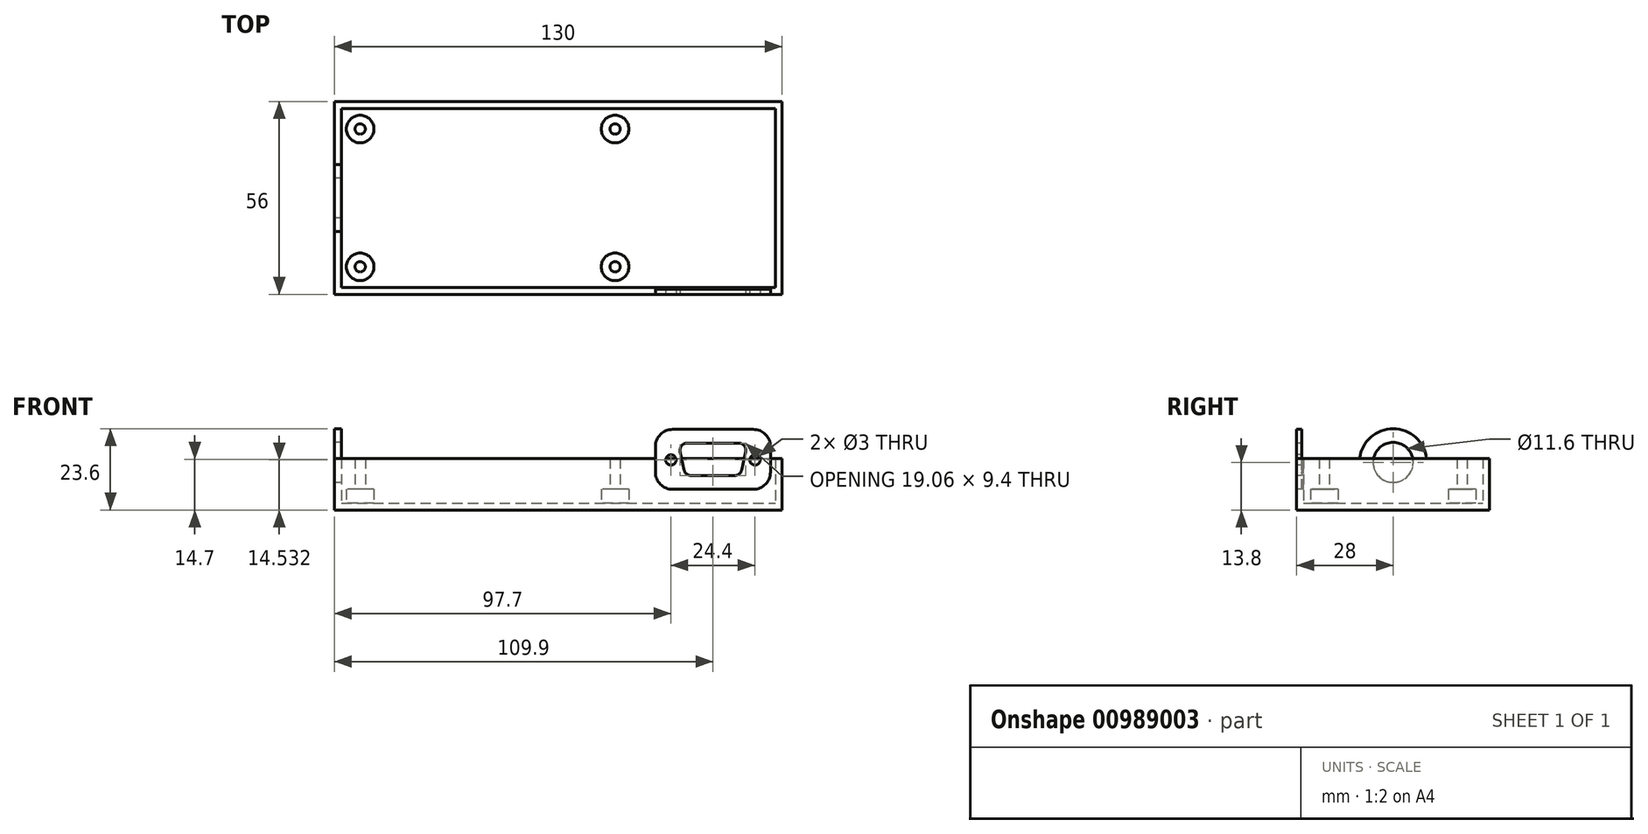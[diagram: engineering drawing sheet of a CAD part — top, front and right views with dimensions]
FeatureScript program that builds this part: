
annotation { "Feature Type Name" : "Feature", "Feature Type Description" : "" }
export const myFeature = defineFeature(function(context is Context, id is Id, definition is map)
    precondition{}
    {
        {
            var Q0;
            Q0=qCreatedBy(makeId("Top.planeOp"),FACE);
            var sketch = newSketch(context, id + "F0", { "sketchPlane" : qUnion([Q0])});
            skLineSegment(sketch, "E0.bottom", {"start": v(0, 0) * mm, "end": v(130, 0) * mm});
            skLineSegment(sketch, "E0.top", {"start": v(0, 56) * mm, "end": v(130, 56) * mm});
            skLineSegment(sketch, "E0.left", {"start": v(0, 0) * mm, "end": v(0, 56) * mm});
            skLineSegment(sketch, "E0.right", {"start": v(130, 0) * mm, "end": v(130, 56) * mm});
            skSolve(sketch);
        }
        {
            var Q0;
            Q0=makeQuery(id+"F0.imprint","IMPRINT",FACE,{"disambiguationData":[TD([[makeQuery(id+"F0.imprint","IMPRINT",EDGE,{"derivedFrom":sQuery(id+"F0.wireOp",EDGE,"E0.bottom")}),1.0]])]});
            extrude(context, id + "F1", {"entities" : qUnion([Q0]), "depth" : 15 * mm, "offsetDistance" : 25 * mm});
        }
        {
            var Q0;
            Q0=makeQuery(id+"F1.opExtrude","CAP_FACE",FACE,{"disambiguationData":[OSD([sQuery(id+"F0.wireOp",EDGE,"E0.bottom"),sQuery(id+"F0.wireOp",EDGE,"E0.top"),sQuery(id+"F0.wireOp",EDGE,"E0.left"),sQuery(id+"F0.wireOp",EDGE,"E0.right")])],"isStart":false});
            shell(context, id + "F2", {"entities" : qUnion([Q0]), "thickness" : 2 * mm});
        }
        {
            var Q0;
            Q0=makeQuery(id+"F2.opShell","OFFSET_FACE",FACE,{"disambiguationData":[OSD([sQuery(id+"F0.wireOp",EDGE,"E0.bottom"),sQuery(id+"F0.wireOp",EDGE,"E0.top"),sQuery(id+"F0.wireOp",EDGE,"E0.left"),sQuery(id+"F0.wireOp",EDGE,"E0.right")])]});
            var sketch = newSketch(context, id + "F3", { "sketchPlane" : qUnion([Q0])});
            skLineSegment(sketch, "E1.bottom", {"start": v(2.5, 53) * mm, "end": v(86.5, 53) * mm, "construction": true});
            skLineSegment(sketch, "E1.top", {"start": v(2.5, 3) * mm, "end": v(86.5, 3) * mm, "construction": true});
            skLineSegment(sketch, "E1.left", {"start": v(2.5, 53) * mm, "end": v(2.5, 3) * mm, "construction": true});
            skLineSegment(sketch, "E1.right", {"start": v(86.5, 53) * mm, "end": v(86.5, 3) * mm, "construction": true});
            skCircle(sketch, "E2", {"center": v(81.5, 48) * mm, "radius": 1.5 * mm});
            skCircle(sketch, "E3", {"center": v(81.5, 8) * mm, "radius": 1.5 * mm});
            skCircle(sketch, "E4", {"center": v(7.5, 8) * mm, "radius": 1.5 * mm});
            skCircle(sketch, "E5", {"center": v(7.5, 48) * mm, "radius": 1.5 * mm});
            skSolve(sketch);
        }
        {
            var Q0;
            Q0 = qSketchRegion(id + "F3", true);
            extrude(context, id + "F4", {"entities" : qUnion([Q0]), "operationType" : NewBodyOperationType.ADD, "depth" : 13 * mm, "offsetDistance" : 25 * mm});
        }
        {
            var Q0;
            Q0=makeQuery(id+"F2.opShell","OFFSET_FACE",FACE,{"disambiguationData":[OSD([sQuery(id+"F0.wireOp",EDGE,"E0.bottom"),sQuery(id+"F0.wireOp",EDGE,"E0.top"),sQuery(id+"F0.wireOp",EDGE,"E0.left"),sQuery(id+"F0.wireOp",EDGE,"E0.right")])]});
            var sketch = newSketch(context, id + "F5", { "sketchPlane" : qUnion([Q0])});
            skCircle(sketch, "E6", {"center": v(81.5, 48) * mm, "radius": 4 * mm});
            skCircle(sketch, "E7", {"center": v(81.5, 8) * mm, "radius": 4 * mm});
            skCircle(sketch, "E8", {"center": v(7.5, 48) * mm, "radius": 4 * mm});
            skCircle(sketch, "E9", {"center": v(7.5, 8) * mm, "radius": 4 * mm});
            skSolve(sketch);
        }
        {
            var Q0;
            Q0 = qSketchRegion(id + "F5", true);
            extrude(context, id + "F6", {"entities" : qUnion([Q0]), "operationType" : NewBodyOperationType.ADD, "depth" : 4 * mm, "offsetDistance" : 25 * mm});
        }
        {
            var Q0;
            Q0=makeQuery(id+"F1.opExtrude","SWEPT_FACE",FACE,{"disambiguationData":[OSD([sQuery(id+"F0.wireOp",EDGE,"E0.bottom")])]});
            var sketch = newSketch(context, id + "F7", { "sketchPlane" : qUnion([Q0])});
            skLineSegment(sketch, "E10", {"start": v(102.37, 19.4) * mm, "end": v(117.43, 19.4) * mm});
            skLineSegment(sketch, "E11", {"start": v(119.39, 16.98) * mm, "end": v(118.24, 11.58) * mm});
            skLineSegment(sketch, "E12", {"start": v(116.28, 10) * mm, "end": v(103.52, 10) * mm});
            skLineSegment(sketch, "E13", {"start": v(101.56, 11.58) * mm, "end": v(100.41, 16.98) * mm});
            skPoint(sketch, "E14.visualSharp", {"position": v(99.9, 19.4) * mm});
            skArc(sketch, "E14.filletArc", {"start": v(102.37, 19.4) * mm, "mid": v(100.82, 18.66) * mm, "end": v(100.41, 16.98) * mm});
            skPoint(sketch, "E15.visualSharp", {"position": v(119.9, 19.4) * mm});
            skArc(sketch, "E15.filletArc", {"start": v(119.39, 16.98) * mm, "mid": v(118.98, 18.66) * mm, "end": v(117.43, 19.4) * mm});
            skPoint(sketch, "E16.visualSharp", {"position": v(117.9, 10) * mm});
            skArc(sketch, "E16.filletArc", {"start": v(116.28, 10) * mm, "mid": v(117.54, 10.45) * mm, "end": v(118.24, 11.58) * mm});
            skPoint(sketch, "E17.visualSharp", {"position": v(101.9, 10) * mm});
            skArc(sketch, "E17.filletArc", {"start": v(101.56, 11.58) * mm, "mid": v(102.26, 10.45) * mm, "end": v(103.52, 10) * mm});
            skCircle(sketch, "E18", {"center": v(97.7, 14.53) * mm, "radius": 1.5 * mm});
            skCircle(sketch, "E19", {"center": v(122.1, 14.53) * mm, "radius": 1.5 * mm});
            skLineSegment(sketch, "E20", {"start": v(109.9, 25.37) * mm, "end": v(109.9, 5.82) * mm, "construction": true});
            skLineSegment(sketch, "E21.bottom", {"start": v(98.2, 23.4) * mm, "end": v(121.6, 23.4) * mm});
            skLineSegment(sketch, "E21.top", {"start": v(98.2, 6) * mm, "end": v(121.6, 6) * mm});
            skLineSegment(sketch, "E21.left", {"start": v(93.2, 18.4) * mm, "end": v(93.2, 11) * mm});
            skLineSegment(sketch, "E21.right", {"start": v(126.6, 18.4) * mm, "end": v(126.6, 11) * mm});
            skPoint(sketch, "E22.visualSharp", {"position": v(126.6, 6) * mm});
            skArc(sketch, "E22.filletArc", {"start": v(121.6, 6) * mm, "mid": v(125.14, 7.46) * mm, "end": v(126.6, 11) * mm});
            skPoint(sketch, "E23.visualSharp", {"position": v(93.2, 6) * mm});
            skArc(sketch, "E23.filletArc", {"start": v(93.2, 11) * mm, "mid": v(94.66, 7.46) * mm, "end": v(98.2, 6) * mm});
            skPoint(sketch, "E24.visualSharp", {"position": v(126.6, 23.4) * mm});
            skArc(sketch, "E24.filletArc", {"start": v(126.6, 18.4) * mm, "mid": v(125.14, 21.94) * mm, "end": v(121.6, 23.4) * mm});
            skPoint(sketch, "E25.visualSharp", {"position": v(93.2, 23.4) * mm});
            skArc(sketch, "E25.filletArc", {"start": v(98.2, 23.4) * mm, "mid": v(94.66, 21.94) * mm, "end": v(93.2, 18.4) * mm});
            skSolve(sketch);
        }
        {
            var Q0;
            Q0=makeQuery(id+"F7.imprint","IMPRINT",FACE,{"disambiguationData":[TD([[makeQuery(id+"F7.imprint","IMPRINT",EDGE,{"derivedFrom":sQuery(id+"F7.wireOp",EDGE,"E12")}),1.0]])]});
            var sketch = newSketch(context, id + "F8", { "sketchPlane" : qUnion([Q0])});
            skLineSegment(sketch, "E26.bottom", {"start": v(93.2, 23.4) * mm, "end": v(126.6, 23.4) * mm});
            skLineSegment(sketch, "E26.top", {"start": v(98.2, 6) * mm, "end": v(121.6, 6) * mm});
            skLineSegment(sketch, "E26.left", {"start": v(93.2, 23.4) * mm, "end": v(93.2, 11) * mm});
            skLineSegment(sketch, "E26.right", {"start": v(126.6, 23.4) * mm, "end": v(126.6, 11) * mm});
            skPoint(sketch, "E27.visualSharp", {"position": v(93.2, 6) * mm});
            skArc(sketch, "E27.filletArc", {"start": v(93.2, 11) * mm, "mid": v(94.66, 7.46) * mm, "end": v(98.2, 6) * mm});
            skPoint(sketch, "E28.visualSharp", {"position": v(126.6, 6) * mm});
            skArc(sketch, "E28.filletArc", {"start": v(121.6, 6) * mm, "mid": v(125.14, 7.46) * mm, "end": v(126.6, 11) * mm});
            skSolve(sketch);
        }
        {
            var Q0;
            Q0 = qSketchRegion(id + "F8", true);
            extrude(context, id + "F9", {"entities" : qUnion([Q0]), "operationType" : NewBodyOperationType.REMOVE, "oppositeDirection" : true, "depth" : 5 * mm, "offsetDistance" : 25 * mm});
        }
        {
            var Q0;
            Q0 = qSketchRegion(id + "F7", true);
            extrude(context, id + "F10", {"entities" : qUnion([Q0]), "oppositeDirection" : true, "depth" : 1.5 * mm, "offsetDistance" : 25 * mm});
        }
        {
            var Q0;
            Q0=makeQuery(id+"F1.opExtrude","SWEPT_FACE",FACE,{"disambiguationData":[OSD([sQuery(id+"F0.wireOp",EDGE,"E0.left")])]});
            var sketch = newSketch(context, id + "F11", { "sketchPlane" : qUnion([Q0])});
            skCircle(sketch, "E29", {"center": v(-28, 13.8) * mm, "radius": 5.8 * mm});
            skSolve(sketch);
        }
        {
            var Q0;
            {var subQ0=sQuery(id+"F11.wireOp",EDGE,"E29");var subQ1=makeQuery(id+"F1.opExtrude","CAP_EDGE",EDGE,{"disambiguationData":[OSD([sQuery(id+"F0.wireOp",EDGE,"E0.left")])],"isStart":false});var subQ2=makeQuery(id+"F11.imprint","INTERSECT",VERTEX,{"disambiguationData":[OD(0.0)],"derivedFrom":[subQ1,subQ0]});Q0=makeQuery(id+"F11.imprint","IMPRINT",FACE,{"disambiguationData":[TD([[makeQuery(id+"F11.imprint","IMPRINT",EDGE,{"disambiguationData":[TD([[subQ2,1.0]])],"derivedFrom":subQ0}),1.0]])]});}
            extrude(context, id + "F12", {"entities" : qUnion([Q0]), "operationType" : NewBodyOperationType.REMOVE, "oppositeDirection" : true, "depth" : 25 * mm, "offsetDistance" : 25 * mm});
        }
        {
            var Q0;
            Q0=makeQuery(id+"F1.opExtrude","SWEPT_FACE",FACE,{"disambiguationData":[OSD([sQuery(id+"F0.wireOp",EDGE,"E0.left")])]});
            var sketch = newSketch(context, id + "F13", { "sketchPlane" : qUnion([Q0])});
            skCircle(sketch, "E30", {"center": v(-28, 13.8) * mm, "radius": 5.8 * mm});
            skCircle(sketch, "E31", {"center": v(-28, 13.8) * mm, "radius": 9.8 * mm});
            skSolve(sketch);
        }
        {
            var Q0;
            {var subQ0=sQuery(id+"F13.wireOp",EDGE,"E30");var subQ1=sQuery(id+"F0.wireOp",EDGE,"E0.bottom");var subQ2=sQuery(id+"F0.wireOp",EDGE,"E0.left");var subQ7=makeQuery(id+"F1.opExtrude","CAP_EDGE",EDGE,{"disambiguationData":[OSD([subQ2])],"isStart":false});var subQ8=makeQuery(id+"F12.boolean.opBoolean","SPLIT",EDGE,{"disambiguationData":[TD([makeQuery(id+"F1.opExtrude","SWEPT_FACE",FACE,{"disambiguationData":[OSD([subQ1])]})])],"derivedFrom":subQ7});var subQ9=makeQuery(id+"F13.imprint","INTERSECT",VERTEX,{"derivedFrom":[subQ8,subQ0]});Q0=makeQuery(id+"F13.imprint","IMPRINT",FACE,{"disambiguationData":[TD([[makeQuery(id+"F13.imprint","IMPRINT",EDGE,{"disambiguationData":[TD([[subQ9,-1.0]])],"derivedFrom":subQ0}),-1.0]])]});}
            extrude(context, id + "F14", {"entities" : qUnion([Q0]), "operationType" : NewBodyOperationType.ADD, "oppositeDirection" : true, "depth" : 2 * mm, "offsetDistance" : 25 * mm});
        }
    });
